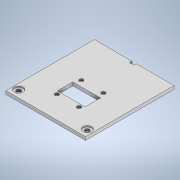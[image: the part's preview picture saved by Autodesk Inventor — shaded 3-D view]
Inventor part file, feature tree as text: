
AUTODESK INVENTOR PART (.ipt)
format: ipt  version: 2021 (Build 250183000, 183)  size: 188,416 bytes
history: native  units: mm
features: thread x6, extrude x3, other x1, sketch x1
ambient origin geometry x8: Origin, YZ Plane, XZ Plane, XY Plane, X Axis, Y Axis, Z Axis, Center Point
bodies: Body1 (feature_tree)
feature tree (11):
  other  "Sólido1"
  sketch  "Boceto1"  dims[d0=36.0mm d1=1.5mm d2=77.0mm d3=1.5mm d4=72.0mm d5=5.0mm d6=5.0mm d7=1.5mm d8=5.0mm d9=5.0mm d10=4.0mm d11=4.0mm d12=3.0mm d13=0.0mm d14=36.0mm d15=2.25mm d16=2.0mm d17=2.0mm d18=50.0mm d19=25.0mm d20=14.0mm d21=5.4mm d22=2.5mm d23=2.5mm d24=2.5mm d25=2.5mm d26=3.5mm d27=3.5mm d28=27.0mm d29=25.0mm d30=2.5mm d31=2.5mm d32=2.5mm d33=2.5mm d34=3.5mm d35=3.5mm d36=1.5mm d37=0.0mm d38=3.0mm d39=0.0mm d40=3.0mm d41=0.0mm d42=1.5mm d43=0.0mm d44=1.5mm d45=0.0mm d46=1.5mm d47=0.0mm d48=1.5mm d49=0.0mm d50=8.0mm d51=8.0mm d52=1.0mm d53=0.0mm]
  extrude  "Extrusión1"  Depth=1.5mm
  extrude  "Extrusión2"  Depth=1.0mm
  thread  "Rosca1"  [1 undecoded]
  thread  "Rosca2"  [1 undecoded]
  thread  "Rosca3"  [1 undecoded]
  thread  "Rosca4"  [1 undecoded]
  thread  "Rosca5"  [1 undecoded]
  thread  "Rosca6"  [1 undecoded]
  extrude  "Extrusión3"  Depth=1.0mm
note: 6 required parameter values undecoded (feature->parameter linkage not recoverable at this tier; creation-order binding heuristic only, values carry confidence <= 0.55)
